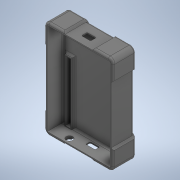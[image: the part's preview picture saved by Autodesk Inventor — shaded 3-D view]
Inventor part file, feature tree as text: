
AUTODESK INVENTOR PART (.ipt)
format: ipt  version: 2020 (Build 240168000, 168)  size: 318,976 bytes
history: native  units: in
note: dims shown in document units (in); Inventor stores cm internally (conversion verified against a paired STEP export)
features: fillet x2, extrude x1, sketch x1, projected_geometry x1, imported_body x1
ambient origin geometry x8: Origin, YZ Plane, XZ Plane, XY Plane, X Axis, Y Axis, Z Axis, Center Point
bodies: Solid1 (feature_tree)
feature tree (6):
  extrude  "Extrusion1"  Depth=0.0787in
  fillet  "Fillet1"  Radius=0.0787in
  fillet  "Fillet2"  [1 undecoded]
  sketch  "Sketch1"  dims[d0=0.3937in d1=0.0in d2=0.0787in d3=0.0787in]
  projected_geometry  "Projected Loop1"
  imported_body  "Base1"
note: 1 required parameter value undecoded (feature->parameter linkage not recoverable at this tier; creation-order binding heuristic only, values carry confidence <= 0.55)
